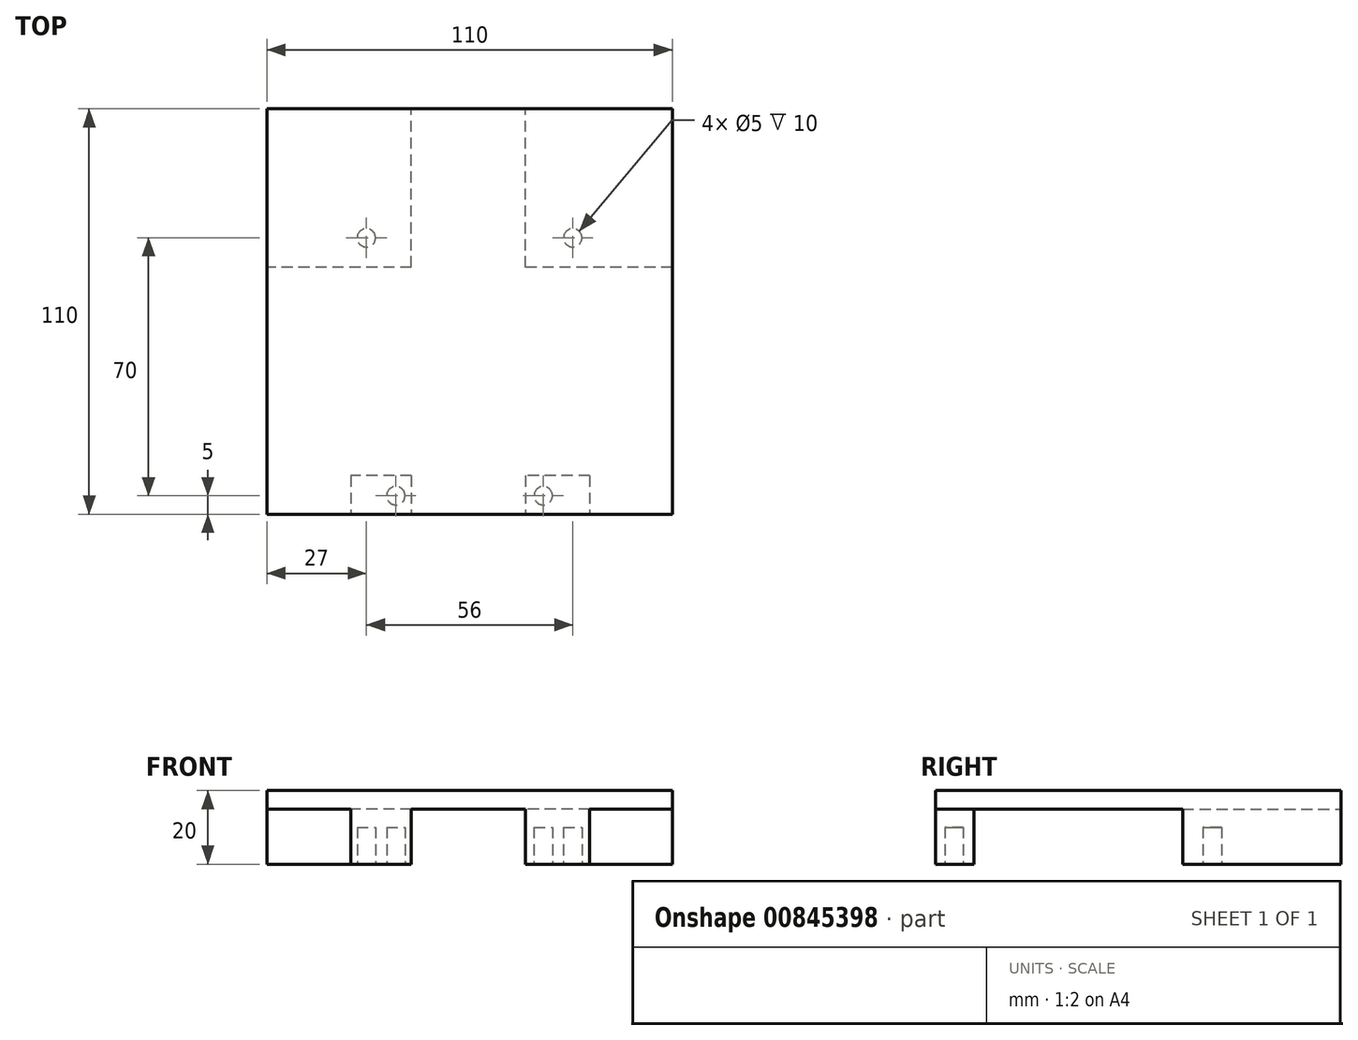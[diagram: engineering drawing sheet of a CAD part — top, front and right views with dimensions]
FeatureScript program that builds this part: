
annotation { "Feature Type Name" : "Feature", "Feature Type Description" : "" }
export const myFeature = defineFeature(function(context is Context, id is Id, definition is map)
    precondition{}
    {
        {
            var Q0;
            Q0=qCreatedBy(makeId("Top.planeOp"),FACE);
            var sketch = newSketch(context, id + "F0", { "sketchPlane" : qUnion([Q0])});
            skLineSegment(sketch, "E0.bottom", {"start": v(-55, -55) * mm, "end": v(55, -55) * mm});
            skLineSegment(sketch, "E0.top", {"start": v(-55, 55) * mm, "end": v(55, 55) * mm});
            skLineSegment(sketch, "E0.left", {"start": v(-55, -55) * mm, "end": v(-55, 55) * mm});
            skLineSegment(sketch, "E0.right", {"start": v(55, -55) * mm, "end": v(55, 55) * mm});
            skPoint(sketch, "E0.middle", {"position": v(0, 0) * mm});
            skSolve(sketch);
        }
        {
            var Q0;
            Q0 = qSketchRegion(id + "F0", true);
            extrude(context, id + "F1", {"entities" : qUnion([Q0]), "depth" : 20 * mm, "offsetDistance" : 25.4 * mm});
        }
        {
            var Q0;
            Q0=makeQuery(id+"F1.opExtrude","CAP_FACE",FACE,{"disambiguationData":[OSD([sQuery(id+"F0.wireOp",EDGE,"E0.bottom"),sQuery(id+"F0.wireOp",EDGE,"E0.top"),sQuery(id+"F0.wireOp",EDGE,"E0.left"),sQuery(id+"F0.wireOp",EDGE,"E0.right")])],"isStart":true});
            var sketch = newSketch(context, id + "F2", { "sketchPlane" : qUnion([Q0])});
            skCircle(sketch, "E1", {"center": v(20, 50) * mm, "radius": 2.5 * mm});
            skCircle(sketch, "E2", {"center": v(-20, 50) * mm, "radius": 2.5 * mm});
            skCircle(sketch, "E3", {"center": v(28, -20) * mm, "radius": 2.5 * mm});
            skCircle(sketch, "E4", {"center": v(-28, -20) * mm, "radius": 2.5 * mm});
            skSolve(sketch);
        }
        {
            var Q0;
            Q0 = qSketchRegion(id + "F2", true);
            extrude(context, id + "F3", {"entities" : qUnion([Q0]), "operationType" : NewBodyOperationType.REMOVE, "oppositeDirection" : true, "depth" : 10 * mm, "offsetDistance" : 25.4 * mm});
        }
        {
            var Q0;
            Q0=makeQuery(id+"F1.opExtrude","CAP_FACE",FACE,{"disambiguationData":[OSD([sQuery(id+"F0.wireOp",EDGE,"E0.bottom"),sQuery(id+"F0.wireOp",EDGE,"E0.top"),sQuery(id+"F0.wireOp",EDGE,"E0.left"),sQuery(id+"F0.wireOp",EDGE,"E0.right")])],"isStart":true});
            var sketch = newSketch(context, id + "F4", { "sketchPlane" : qUnion([Q0])});
            skLineSegment(sketch, "E5.bottom", {"start": v(55, -12) * mm, "end": v(15.19, -12) * mm});
            skLineSegment(sketch, "E5.top", {"start": v(32.58, 44.57) * mm, "end": v(15.19, 44.57) * mm});
            skLineSegment(sketch, "E5.left", {"start": v(55, -12) * mm, "end": v(55, 44.57) * mm});
            skLineSegment(sketch, "E5.right", {"start": v(-55, -12) * mm, "end": v(-55, 44.57) * mm});
            skLineSegment(sketch, "E6.top", {"start": v(15.19, 55) * mm, "end": v(-15.79, 55) * mm});
            skLineSegment(sketch, "E6.left", {"start": v(15.19, 44.57) * mm, "end": v(15.19, 55) * mm});
            skLineSegment(sketch, "E6.right", {"start": v(-15.79, 44.57) * mm, "end": v(-15.79, 55) * mm});
            skLineSegment(sketch, "E7.trimOffspring", {"start": v(-15.79, 44.57) * mm, "end": v(-32.2, 44.57) * mm});
            skLineSegment(sketch, "E8.bottom", {"start": v(15.19, 44.57) * mm, "end": v(-15.79, 44.57) * mm});
            skLineSegment(sketch, "E8.top", {"start": v(15.19, -55) * mm, "end": v(-15.79, -55) * mm});
            skLineSegment(sketch, "E8.left", {"start": v(15.19, -12) * mm, "end": v(15.19, -55) * mm});
            skLineSegment(sketch, "E8.right", {"start": v(-15.79, -12) * mm, "end": v(-15.79, -55) * mm});
            skLineSegment(sketch, "E9.top", {"start": v(-55, 55) * mm, "end": v(-32.2, 55) * mm});
            skLineSegment(sketch, "E9.left", {"start": v(-55, 44.57) * mm, "end": v(-55, 55) * mm});
            skLineSegment(sketch, "E9.right", {"start": v(-32.2, 44.57) * mm, "end": v(-32.2, 55) * mm});
            skLineSegment(sketch, "E10.top", {"start": v(55, 55) * mm, "end": v(32.58, 55) * mm});
            skLineSegment(sketch, "E10.left", {"start": v(55, 44.57) * mm, "end": v(55, 55) * mm});
            skLineSegment(sketch, "E10.right", {"start": v(32.58, 44.57) * mm, "end": v(32.58, 55) * mm});
            skLineSegment(sketch, "E11.trimOffspring", {"start": v(-15.79, -12) * mm, "end": v(-55, -12) * mm});
            skSolve(sketch);
        }
        {
            var Q0;
            Q0 = qSketchRegion(id + "F4", true);
            extrude(context, id + "F5", {"entities" : qUnion([Q0]), "operationType" : NewBodyOperationType.REMOVE, "oppositeDirection" : true, "depth" : 15 * mm, "offsetDistance" : 25.4 * mm});
        }
    });
